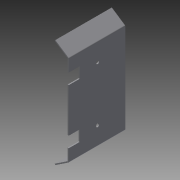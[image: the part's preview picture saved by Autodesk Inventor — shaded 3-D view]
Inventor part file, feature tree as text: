
AUTODESK INVENTOR PART (.ipt)
format: ipt  version: 2015 (Build 190159000, 159)  size: 111,104 bytes
history: native  units: mm
features: extrude x3, sketch x2
ambient origin geometry x8: Origin, YZ Plane, XZ Plane, XY Plane, X Axis, Y Axis, Z Axis, Center Point
bodies: Solid1 (feature_tree)
feature tree (5):
  extrude  "Extrusion1"  Depth=1.0mm
  sketch  "Sketch2"  dims[d5=52.0mm d6=0.0mm d10=3.0mm d11=3.0mm d12=1.0mm d13=0.0mm d14=5.0mm d15=5.0mm d16=10.0mm d17=10.0mm d18=10.0mm d19=10.0mm d20=1.0mm d21=0.0mm]
  extrude  "Extrusion2"  Depth=1.0mm
  extrude  "Extrusion3"  Depth=1.0mm
  sketch  "Sketch1"  dims[d0=1.0mm d4=1.0mm]
